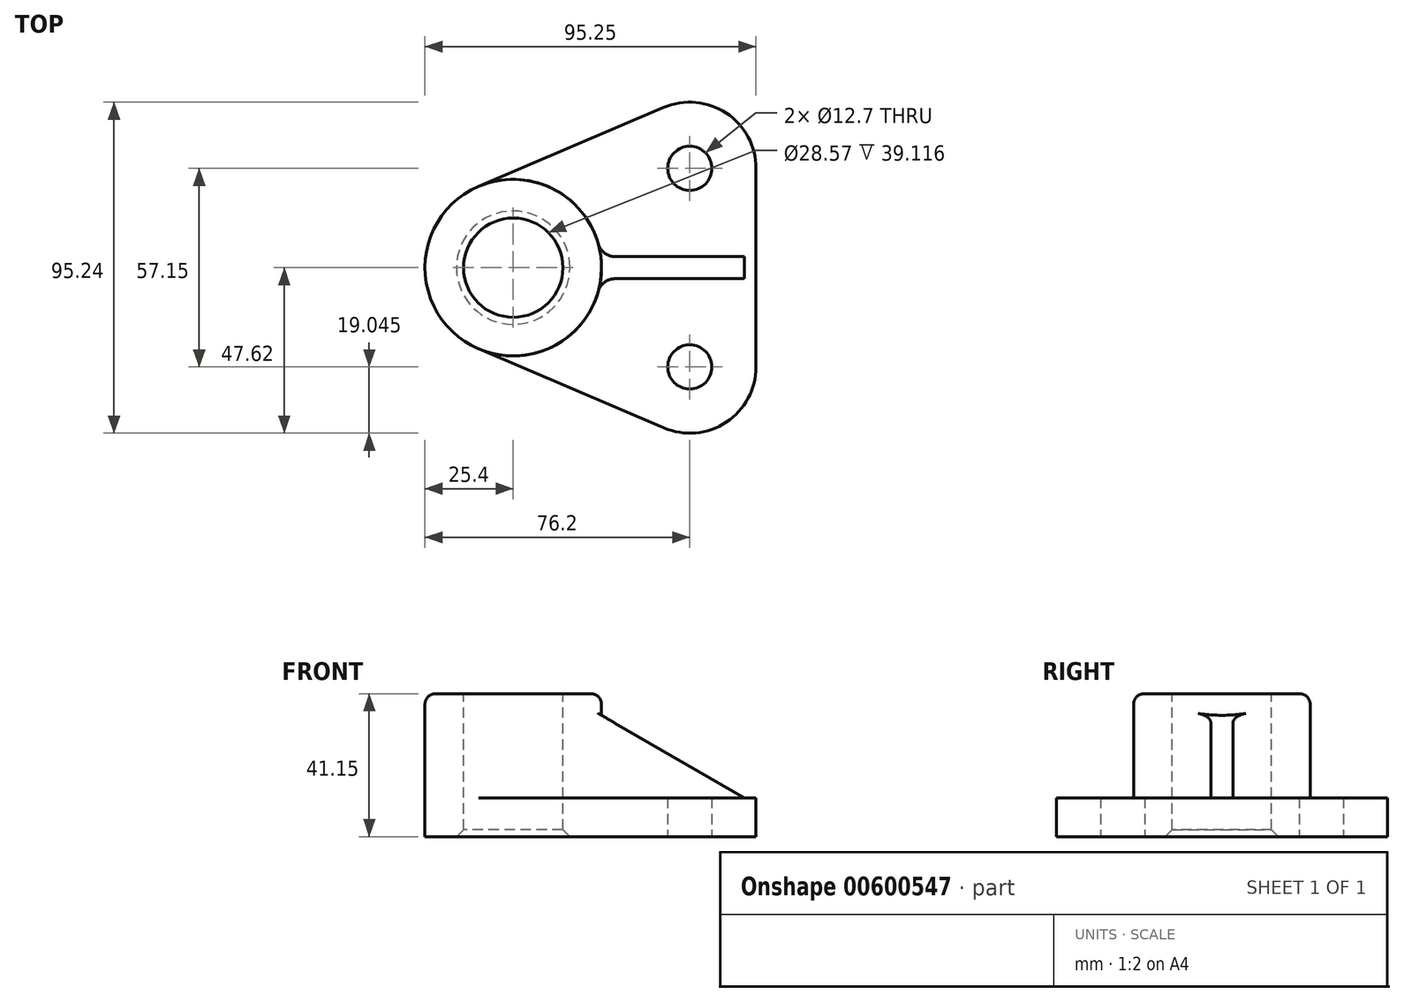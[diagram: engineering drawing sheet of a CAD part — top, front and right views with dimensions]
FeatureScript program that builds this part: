
annotation { "Feature Type Name" : "Feature", "Feature Type Description" : "" }
export const myFeature = defineFeature(function(context is Context, id is Id, definition is map)
    precondition{}
    {
        {
            var Q0;
            Q0=qCreatedBy(makeId("Top.planeOp"),FACE);
            var sketch = newSketch(context, id + "F0", { "sketchPlane" : qUnion([Q0])});
            skArc(sketch, "E0", {"start": v(-9.97, 23.36) * mm, "mid": v(-25.4, 0) * mm, "end": v(-9.97, -23.36) * mm});
            skArc(sketch, "E1", {"start": v(69.85, 28.57) * mm, "mid": v(61.3, 44.47) * mm, "end": v(43.33, 46.1) * mm});
            skArc(sketch, "E2", {"start": v(43.33, -46.1) * mm, "mid": v(61.3, -44.47) * mm, "end": v(69.85, -28.57) * mm});
            skLineSegment(sketch, "E3", {"start": v(-9.97, 23.36) * mm, "end": v(43.33, 46.1) * mm});
            skLineSegment(sketch, "E4", {"start": v(0, 0) * mm, "end": v(50.8, 0) * mm, "construction": true});
            skLineSegment(sketch, "E5", {"start": v(50.8, 28.57) * mm, "end": v(50.8, -28.57) * mm, "construction": true});
            skLineSegment(sketch, "E6", {"start": v(43.33, -46.1) * mm, "end": v(-9.97, -23.36) * mm});
            skLineSegment(sketch, "E7", {"start": v(69.85, 28.57) * mm, "end": v(69.85, -28.57) * mm});
            skCircle(sketch, "E8", {"center": v(50.8, 28.57) * mm, "radius": 6.35 * mm});
            skCircle(sketch, "E9", {"center": v(50.8, -28.57) * mm, "radius": 6.35 * mm});
            skSolve(sketch);
        }
        {
            var Q0;
            Q0 = qSketchRegion(id + "F0", true);
            extrude(context, id + "F1", {"entities" : qUnion([Q0]), "depth" : (0.44 * 25.4) * mm, "offsetDistance" : 25 * mm});
        }
        {
            var Q0;
            Q0=makeQuery(id+"F1.opExtrude","CAP_FACE",FACE,{"disambiguationData":[OSD([sQuery(id+"F0.wireOp",EDGE,"E0"),sQuery(id+"F0.wireOp",EDGE,"E1"),sQuery(id+"F0.wireOp",EDGE,"E2"),sQuery(id+"F0.wireOp",EDGE,"E3"),sQuery(id+"F0.wireOp",EDGE,"E6"),sQuery(id+"F0.wireOp",EDGE,"E7"),sQuery(id+"F0.wireOp",EDGE,"E8"),sQuery(id+"F0.wireOp",EDGE,"E9")])],"isStart":false});
            var sketch = newSketch(context, id + "F2", { "sketchPlane" : qUnion([Q0])});
            skCircle(sketch, "E10", {"center": v(0, 0) * mm, "radius": 25.4 * mm});
            skSolve(sketch);
        }
        {
            var Q0;
            {var subQ0=sQuery(id+"F2.wireOp",EDGE,"E10");var subQ1=makeQuery(id+"F2.imprint","INTERSECT",VERTEX,{"derivedFrom":[makeQuery(id+"F1.opExtrude","CAP_EDGE",EDGE,{"disambiguationData":[OSD([sQuery(id+"F0.wireOp",EDGE,"E3")])],"isStart":false}),subQ0]});Q0=makeQuery(id+"F2.imprint","IMPRINT",FACE,{"disambiguationData":[TD([[makeQuery(id+"F2.imprint","IMPRINT",EDGE,{"disambiguationData":[TD([[subQ1,-1.0]])],"derivedFrom":subQ0}),1.0]])]});}
            extrude(context, id + "F3", {"entities" : qUnion([Q0]), "operationType" : NewBodyOperationType.ADD, "depth" : ((1.62 - 0.44) * 25.4) * mm, "offsetDistance" : 25 * mm});
        }
        {
            var Q0;
            Q0=qCreatedBy(makeId("Front.planeOp"),FACE);
            var sketch = newSketch(context, id + "F4", { "sketchPlane" : qUnion([Q0])});
            skLineSegment(sketch, "E11", {"start": v(66.55, 11.18) * mm, "end": v(20, 11.18) * mm});
            skLineSegment(sketch, "E12", {"start": v(20, 11.18) * mm, "end": v(20, 38.05) * mm});
            skLineSegment(sketch, "E13", {"start": v(20, 38.05) * mm, "end": v(66.55, 11.18) * mm});
            skSolve(sketch);
        }
        {
            var Q0;
            Q0=makeQuery(id+"F4.imprint","IMPRINT",FACE,{"disambiguationData":[TD([[makeQuery(id+"F4.imprint","IMPRINT",EDGE,{"derivedFrom":sQuery(id+"F4.wireOp",EDGE,"E11")}),-1.0]])]});
            extrude(context, id + "F5", {"entities" : qUnion([Q0]), "operationType" : NewBodyOperationType.ADD, "endBound" : BoundingType.SYMMETRIC, "depth" : (0.25 * 25.4) * mm, "offsetDistance" : 25 * mm});
        }
        {
            var Q0;
            Q0=makeQuery(id+"F3.opExtrude","CAP_FACE",FACE,{"disambiguationData":[OSD([sQuery(id+"F2.wireOp",EDGE,"E10")])],"isStart":false});
            var sketch = newSketch(context, id + "F6", { "sketchPlane" : qUnion([Q0])});
            skCircle(sketch, "E14", {"center": v(0, 0) * mm, "radius": 14.29 * mm});
            skSolve(sketch);
        }
        {
            var Q0;
            Q0=makeQuery(id+"F6.imprint","IMPRINT",FACE,{"disambiguationData":[TD([[makeQuery(id+"F6.imprint","IMPRINT",EDGE,{"derivedFrom":sQuery(id+"F6.wireOp",EDGE,"E14")}),1.0]])]});
            extrude(context, id + "F7", {"entities" : qUnion([Q0]), "operationType" : NewBodyOperationType.REMOVE, "endBound" : BoundingType.THROUGH_ALL, "oppositeDirection" : true, "depth" : 25 * mm, "offsetDistance" : 25 * mm});
        }
        {
            var Q0;
            {var subQ0=sQuery(id+"F2.wireOp",EDGE,"E10");var subQ1=sQuery(id+"F0.wireOp",EDGE,"E6");Q0=makeQuery(id+"F5.boolean.opBoolean","SPLIT",EDGE,{"disambiguationData":[TD([makeQuery(id+"F1.opExtrude","SWEPT_FACE",FACE,{"disambiguationData":[OSD([subQ1])]})])],"derivedFrom":makeQuery(id+"F3.opExtrude","CAP_EDGE",EDGE,{"disambiguationData":[OSD([subQ0])],"isStart":true})});}
            var Q1;
            Q1=makeQuery(id+"F5.boolean.opBoolean","INTERSECT",EDGE,{"derivedFrom":[makeQuery(id+"F3.boolean.opBoolean","MERGE",FACE,{"derivedFrom":[makeQuery(id+"F1.opExtrude","SWEPT_FACE",FACE,{"disambiguationData":[OSD([sQuery(id+"F0.wireOp",EDGE,"E0")])]}),makeQuery(id+"F3.opExtrude","SWEPT_FACE",FACE,{"disambiguationData":[OSD([sQuery(id+"F2.wireOp",EDGE,"E10")])]})]}),makeQuery(id+"F5.opExtrude","CAP_FACE",FACE,{"disambiguationData":[OSD([sQuery(id+"F4.wireOp",EDGE,"E11"),sQuery(id+"F4.wireOp",EDGE,"E12"),sQuery(id+"F4.wireOp",EDGE,"E13")])],"isStart":false})]});
            var Q2;
            Q2=makeQuery(id+"F5.opExtrude","CAP_EDGE",EDGE,{"disambiguationData":[OSD([sQuery(id+"F4.wireOp",EDGE,"E11")])],"isStart":false});
            var Q3;
            Q3=makeQuery(id+"F5.boolean.opBoolean","INTERSECT",EDGE,{"derivedFrom":[makeQuery(id+"F3.boolean.opBoolean","MERGE",FACE,{"derivedFrom":[makeQuery(id+"F1.opExtrude","SWEPT_FACE",FACE,{"disambiguationData":[OSD([sQuery(id+"F0.wireOp",EDGE,"E0")])]}),makeQuery(id+"F3.opExtrude","SWEPT_FACE",FACE,{"disambiguationData":[OSD([sQuery(id+"F2.wireOp",EDGE,"E10")])]})]}),makeQuery(id+"F5.opExtrude","CAP_FACE",FACE,{"disambiguationData":[OSD([sQuery(id+"F4.wireOp",EDGE,"E11"),sQuery(id+"F4.wireOp",EDGE,"E12"),sQuery(id+"F4.wireOp",EDGE,"E13")])],"isStart":true})]});
            var Q4;
            Q4=makeQuery(id+"F5.opExtrude","CAP_EDGE",EDGE,{"disambiguationData":[OSD([sQuery(id+"F4.wireOp",EDGE,"E11")])],"isStart":true});
            var Q5;
            {var subQ0=sQuery(id+"F2.wireOp",EDGE,"E10");var subQ1=sQuery(id+"F0.wireOp",EDGE,"E3");Q5=makeQuery(id+"F5.boolean.opBoolean","SPLIT",EDGE,{"disambiguationData":[TD([makeQuery(id+"F1.opExtrude","SWEPT_FACE",FACE,{"disambiguationData":[OSD([subQ1])]})])],"derivedFrom":makeQuery(id+"F3.opExtrude","CAP_EDGE",EDGE,{"disambiguationData":[OSD([subQ0])],"isStart":true})});}
            fillet(context, id + "F8", {"entities" : qUnion([Q0, Q1, Q2, Q3, Q4, Q5]), "radius" : (0.2 * 25.4) * mm, "tangentPropagation" : true, "allowEdgeOverflow" : false});
        }
        {
            var Q0;
            Q0=makeQuery(id+"F3.opExtrude","CAP_EDGE",EDGE,{"disambiguationData":[OSD([sQuery(id+"F2.wireOp",EDGE,"E10")])],"isStart":false});
            fillet(context, id + "F9", {"entities" : qUnion([Q0]), "radius" : (0.12 * 25.4) * mm, "tangentPropagation" : true, "allowEdgeOverflow" : false});
        }
        {
            var Q0;
            Q0=makeQuery(id+"F7.boolean.opBoolean","COPY",EDGE,{"derivedFrom":makeQuery(id+"F7.opExtrude","CAP_EDGE",EDGE,{"disambiguationData":[OSD([sQuery(id+"F6.wireOp",EDGE,"E14")])],"isStart":true})});
            var Q1;
            Q1=makeQuery(id+"F7.boolean.opBoolean","INTERSECT",EDGE,{"derivedFrom":[makeQuery(id+"F1.opExtrude","CAP_FACE",FACE,{"disambiguationData":[OSD([sQuery(id+"F0.wireOp",EDGE,"E0"),sQuery(id+"F0.wireOp",EDGE,"E1"),sQuery(id+"F0.wireOp",EDGE,"E2"),sQuery(id+"F0.wireOp",EDGE,"E3"),sQuery(id+"F0.wireOp",EDGE,"E6"),sQuery(id+"F0.wireOp",EDGE,"E7"),sQuery(id+"F0.wireOp",EDGE,"E8"),sQuery(id+"F0.wireOp",EDGE,"E9")])],"isStart":true}),makeQuery(id+"F7.opExtrude","SWEPT_FACE",FACE,{"disambiguationData":[OSD([sQuery(id+"F6.wireOp",EDGE,"E14")])]})]});
            chamfer(context, id + "F10", {"entities" : qUnion([Q0, Q1]), "chamferType" : ChamferType.OFFSET_ANGLE, "width" : (0.08 * 25.4) * mm, "oppositeDirection" : false, "angle" : 45 * degree, "tangentPropagation" : true});
        }
    });
